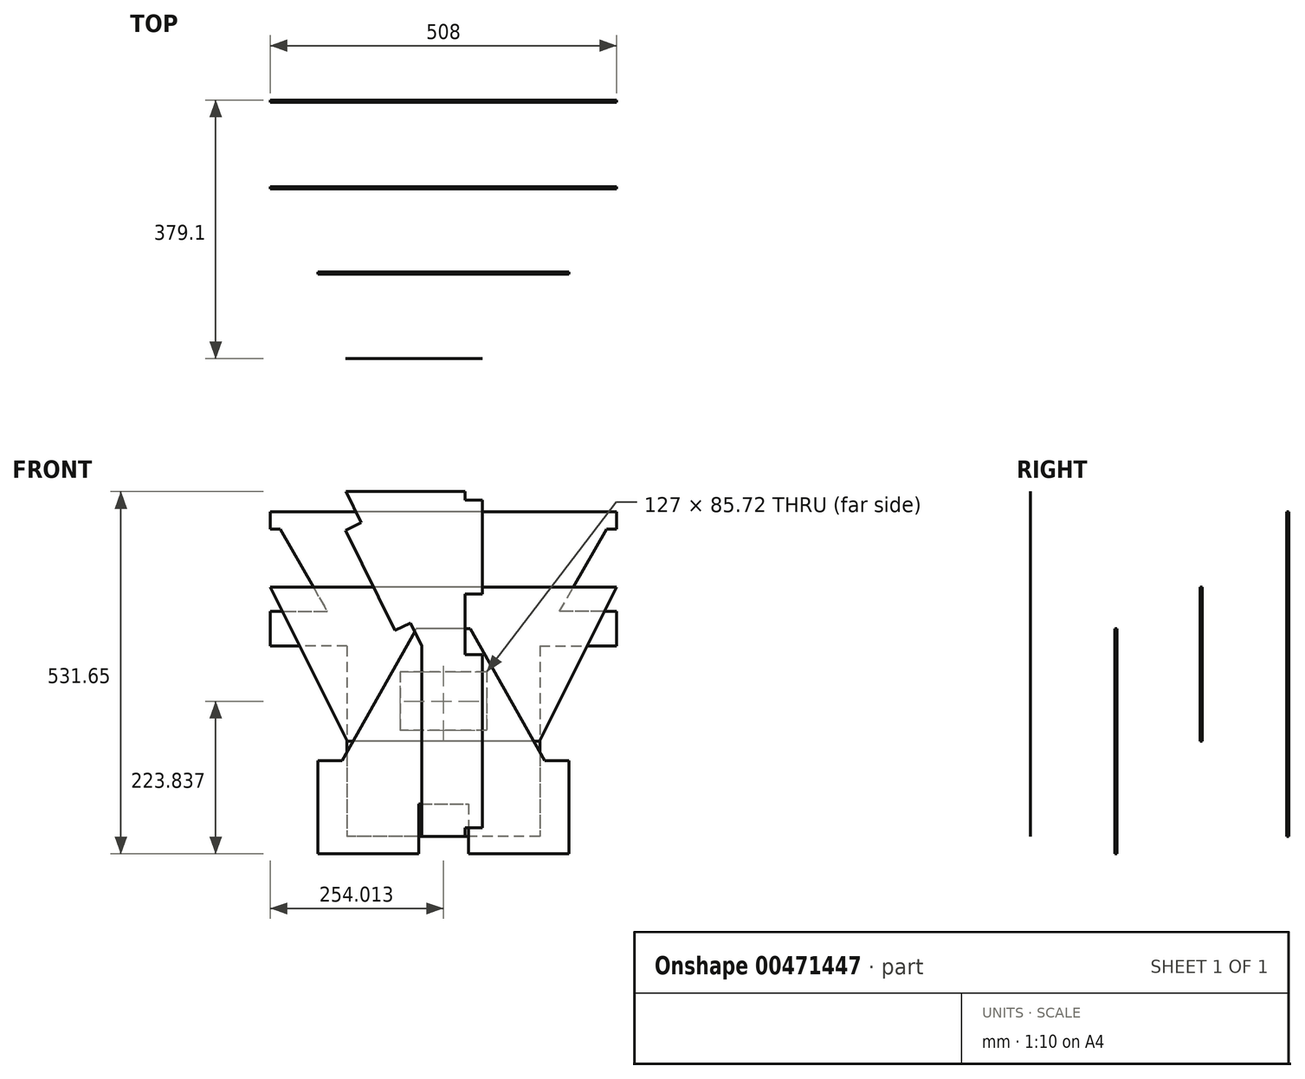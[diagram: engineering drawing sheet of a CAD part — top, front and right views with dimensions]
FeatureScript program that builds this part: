
annotation { "Feature Type Name" : "Feature", "Feature Type Description" : "" }
export const myFeature = defineFeature(function(context is Context, id is Id, definition is map)
    precondition{}
    {
        {
            var Q0;
            Q0=qCreatedBy(makeId("Front.planeOp"),FACE);
            var sketch = newSketch(context, id + "F0", { "sketchPlane" : qUnion([Q0])});
            skPoint(sketch, "E0.middle", {"position": v(0, 0) * mm});
            skLineSegment(sketch, "E1.bottom", {"start": v(-36.51, 165.1) * mm, "end": v(36.51, 165.1) * mm});
            skLineSegment(sketch, "E1.left", {"start": v(-36.51, -92.08) * mm, "end": v(-36.51, -165.1) * mm});
            skLineSegment(sketch, "E1.right", {"start": v(36.51, -92.08) * mm, "end": v(36.51, -165.1) * mm});
            skLineSegment(sketch, "E2", {"start": v(0, 165.1) * mm, "end": v(0, -165.1) * mm, "construction": true});
            skLineSegment(sketch, "E3", {"start": v(-148.48, -28.58) * mm, "end": v(-39.69, 165.1) * mm});
            skLineSegment(sketch, "E4", {"start": v(-36.51, -92.08) * mm, "end": v(36.51, -92.08) * mm});
            skLineSegment(sketch, "E5", {"start": v(-184.15, -92.08) * mm, "end": v(-184.15, -165.1) * mm});
            skLineSegment(sketch, "E6", {"start": v(-184.15, -165.1) * mm, "end": v(-36.51, -165.1) * mm});
            skLineSegment(sketch, "E7", {"start": v(-36.51, -165.1) * mm, "end": v(-36.51, -92.08) * mm});
            skLineSegment(sketch, "E8", {"start": v(-184.15, -92.08) * mm, "end": v(-184.15, -28.58) * mm});
            skLineSegment(sketch, "E9", {"start": v(-184.15, -28.58) * mm, "end": v(-148.48, -28.58) * mm});
            skLineSegment(sketch, "E10.MirrorCS", {"start": v(184.15, -165.1) * mm, "end": v(36.51, -165.1) * mm});
            skLineSegment(sketch, "E11.MirrorCS", {"start": v(36.51, -165.1) * mm, "end": v(36.51, -92.08) * mm});
            skLineSegment(sketch, "E12.MirrorCS", {"start": v(184.15, -92.08) * mm, "end": v(184.15, -165.1) * mm});
            skLineSegment(sketch, "E13.MirrorCS", {"start": v(184.15, -92.08) * mm, "end": v(184.15, -28.58) * mm});
            skLineSegment(sketch, "E14.MirrorCS", {"start": v(148.48, -28.58) * mm, "end": v(39.69, 165.1) * mm});
            skLineSegment(sketch, "E15.MirrorCS", {"start": v(184.15, -28.58) * mm, "end": v(148.48, -28.58) * mm});
            skLineSegment(sketch, "E16.MirrorCS", {"start": v(39.69, 165.1) * mm, "end": v(-39.69, 165.1) * mm});
            skLineSegment(sketch, "E17.MirrorCS", {"start": v(36.51, -92.08) * mm, "end": v(-36.51, -92.08) * mm});
            skPoint(sketch, "E18.MirrorCS.end.orphan", {"position": v(-36.51, -165.1) * mm});
            skPoint(sketch, "E19.orphan", {"position": v(36.51, 165.1) * mm});
            skPoint(sketch, "E20.orphan", {"position": v(-36.51, 165.1) * mm});
            skSolve(sketch);
        }
        {
            var Q0;
            {var subQ1=sQuery(id+"F0.wireOp",EDGE,"E3");Q0=makeQuery(id+"F0.imprint","IMPRINT",FACE,{"disambiguationData":[TD([[makeQuery(id+"F0.imprint","IMPRINT",EDGE,{"derivedFrom":subQ1}),-1.0]])]});}
            extrude(context, id + "F1", {"entities" : qUnion([Q0]), "depth" : 3.17 * mm});
        }
        {
            var Q0;
            Q0=makeQuery(id+"F1.opExtrude","CAP_FACE",FACE,{"disambiguationData":[OSD([sQuery(id+"F0.wireOp",EDGE,"E3"),sQuery(id+"F0.wireOp",EDGE,"E5"),sQuery(id+"F0.wireOp",EDGE,"E6"),sQuery(id+"F0.wireOp",EDGE,"E7"),sQuery(id+"F0.wireOp",EDGE,"E8"),sQuery(id+"F0.wireOp",EDGE,"E9"),sQuery(id+"F0.wireOp",EDGE,"E10.MirrorCS"),sQuery(id+"F0.wireOp",EDGE,"E12.MirrorCS"),sQuery(id+"F0.wireOp",EDGE,"E13.MirrorCS"),sQuery(id+"F0.wireOp",EDGE,"E14.MirrorCS"),sQuery(id+"F0.wireOp",EDGE,"E1.right"),sQuery(id+"F0.wireOp",EDGE,"E15.MirrorCS"),sQuery(id+"F0.wireOp",EDGE,"E16.MirrorCS"),sQuery(id+"F0.wireOp",EDGE,"E17.MirrorCS")])],"isStart":true});
            cPlane(context, id + "F2", {"entities" : qUnion([Q0]), "cplaneType" : CPlaneType.OFFSET, "offset" : 127 * mm, "oppositeDirection" : true, "width" : 152.4 * mm, "height" : 152.4 * mm});
        }
        {
            var Q0;
            Q0=qCreatedBy(id+"F2.planeOp",FACE);
            var sketch = newSketch(context, id + "F3", { "sketchPlane" : qUnion([Q0])});
            skLineSegment(sketch, "E21.bottom", {"start": v(31.75, 139.7) * mm, "end": v(-31.75, 139.7) * mm});
            skLineSegment(sketch, "E21.top", {"start": v(31.75, -139.7) * mm, "end": v(-31.75, -139.7) * mm});
            skLineSegment(sketch, "E21.left", {"start": v(31.75, 139.7) * mm, "end": v(31.75, -139.7) * mm});
            skLineSegment(sketch, "E21.right", {"start": v(-31.75, 139.7) * mm, "end": v(-31.75, -139.7) * mm});
            skPoint(sketch, "E21.middle", {"position": v(0, 0) * mm});
            skLineSegment(sketch, "E22", {"start": v(-31.75, 139.7) * mm, "end": v(-31.75, 366.55) * mm});
            skLineSegment(sketch, "E23", {"start": v(-31.75, 366.55) * mm, "end": v(142.87, 366.55) * mm});
            skLineSegment(sketch, "E24", {"start": v(142.87, 366.55) * mm, "end": v(31.75, 139.7) * mm});
            skLineSegment(sketch, "E25", {"start": v(-31.75, 353.85) * mm, "end": v(-57.15, 353.85) * mm});
            skLineSegment(sketch, "E26", {"start": v(-57.15, 353.85) * mm, "end": v(-57.15, 215.9) * mm});
            skLineSegment(sketch, "E27", {"start": v(-57.15, 215.9) * mm, "end": v(-31.75, 215.9) * mm});
            skLineSegment(sketch, "E28", {"start": v(-31.75, 127) * mm, "end": v(-57.15, 127) * mm});
            skLineSegment(sketch, "E29", {"start": v(-57.15, 127) * mm, "end": v(-57.15, -127) * mm});
            skLineSegment(sketch, "E30", {"start": v(-57.15, -127) * mm, "end": v(-31.75, -127) * mm});
            skLineSegment(sketch, "E31", {"start": v(120.53, 320.93) * mm, "end": v(143.34, 309.75) * mm});
            skLineSegment(sketch, "E32", {"start": v(143.34, 309.75) * mm, "end": v(71.32, 162.74) * mm});
            skLineSegment(sketch, "E33", {"start": v(71.32, 162.74) * mm, "end": v(48.51, 173.92) * mm});
            skSolve(sketch);
        }
        {
            var Q0;
            Q0 = qSketchRegion(id + "F3", true);
            extrude(context, id + "F4", {"entities" : qUnion([Q0]), "depth" : 1 / 203.2 * mm});
        }
        {
            var Q0;
            Q0=makeQuery(id+"F1.opExtrude","CAP_FACE",FACE,{"disambiguationData":[OSD([sQuery(id+"F0.wireOp",EDGE,"E3"),sQuery(id+"F0.wireOp",EDGE,"E5"),sQuery(id+"F0.wireOp",EDGE,"E6"),sQuery(id+"F0.wireOp",EDGE,"E7"),sQuery(id+"F0.wireOp",EDGE,"E8"),sQuery(id+"F0.wireOp",EDGE,"E9"),sQuery(id+"F0.wireOp",EDGE,"E10.MirrorCS"),sQuery(id+"F0.wireOp",EDGE,"E12.MirrorCS"),sQuery(id+"F0.wireOp",EDGE,"E13.MirrorCS"),sQuery(id+"F0.wireOp",EDGE,"E14.MirrorCS"),sQuery(id+"F0.wireOp",EDGE,"E1.right"),sQuery(id+"F0.wireOp",EDGE,"E15.MirrorCS"),sQuery(id+"F0.wireOp",EDGE,"E16.MirrorCS"),sQuery(id+"F0.wireOp",EDGE,"E17.MirrorCS")])],"isStart":true});
            cPlane(context, id + "F5", {"entities" : qUnion([Q0]), "cplaneType" : CPlaneType.OFFSET, "offset" : 121.92 * mm, "width" : 152.4 * mm, "height" : 152.4 * mm});
        }
        {
            var Q0;
            Q0=qCreatedBy(id+"F5.planeOp",FACE);
            var sketch = newSketch(context, id + "F6", { "sketchPlane" : qUnion([Q0])});
            skPoint(sketch, "E34.middle", {"position": v(0, 0) * mm});
            skLineSegment(sketch, "E35", {"start": v(0, 0) * mm, "end": v(0, 226.05) * mm, "construction": true});
            skLineSegment(sketch, "E36", {"start": v(0, 226.05) * mm, "end": v(-254, 226.05) * mm});
            skLineSegment(sketch, "E37", {"start": v(-254, 226.05) * mm, "end": v(-140.92, 0) * mm});
            skLineSegment(sketch, "E38", {"start": v(-140.92, 0) * mm, "end": v(0, 0) * mm});
            skLineSegment(sketch, "E39.MirrorCS", {"start": v(140.92, 0) * mm, "end": v(0, 0) * mm});
            skLineSegment(sketch, "E40.MirrorCS", {"start": v(0, 226.05) * mm, "end": v(254, 226.05) * mm});
            skLineSegment(sketch, "E41.MirrorCS", {"start": v(254, 226.05) * mm, "end": v(140.92, 0) * mm});
            skSolve(sketch);
        }
        {
            var Q0;
            Q0=makeQuery(id+"F6.imprint","IMPRINT",FACE,{"disambiguationData":[TD([[makeQuery(id+"F6.imprint","IMPRINT",EDGE,{"derivedFrom":sQuery(id+"F6.wireOp",EDGE,"E36")}),1.0]])]});
            extrude(context, id + "F7", {"entities" : qUnion([Q0]), "depth" : 3.17 * mm});
        }
        {
            var Q0;
            Q0=qCreatedBy(id+"F5.planeOp",FACE);
            cPlane(context, id + "F8", {"entities" : qUnion([Q0]), "cplaneType" : CPlaneType.OFFSET, "offset" : 127 * mm, "width" : 152.4 * mm, "height" : 152.4 * mm});
        }
        {
            var Q0;
            Q0=qCreatedBy(id+"F8.planeOp",FACE);
            var sketch = newSketch(context, id + "F9", { "sketchPlane" : qUnion([Q0])});
            skLineSegment(sketch, "E42.bottom", {"start": v(-141.29, 139.7) * mm, "end": v(141.29, 139.7) * mm});
            skLineSegment(sketch, "E42.top", {"start": v(-141.29, -139.7) * mm, "end": v(141.29, -139.7) * mm});
            skLineSegment(sketch, "E42.left", {"start": v(-141.29, 139.7) * mm, "end": v(-141.29, -139.7) * mm});
            skLineSegment(sketch, "E42.right", {"start": v(141.29, 139.7) * mm, "end": v(141.29, -139.7) * mm});
            skPoint(sketch, "E42.middle", {"position": v(0, 0) * mm});
            skLineSegment(sketch, "E43", {"start": v(-141.29, 139.7) * mm, "end": v(-254, 336.55) * mm});
            skLineSegment(sketch, "E44", {"start": v(-254, 336.55) * mm, "end": v(254, 336.55) * mm});
            skLineSegment(sketch, "E45", {"start": v(254, 336.55) * mm, "end": v(141.29, 139.7) * mm});
            skLineSegment(sketch, "E46", {"start": v(-63.51, 15.88) * mm, "end": v(-0.01, 15.88) * mm});
            skLineSegment(sketch, "E47", {"start": v(-63.51, 101.6) * mm, "end": v(-0.01, 101.6) * mm});
            skLineSegment(sketch, "E48", {"start": v(0, -139.7) * mm, "end": v(0, 139.7) * mm, "construction": true});
            skLineSegment(sketch, "E49", {"start": v(-0.01, 15.88) * mm, "end": v(63.49, 15.88) * mm});
            skLineSegment(sketch, "E50", {"start": v(-0.01, 101.6) * mm, "end": v(63.49, 101.6) * mm});
            skLineSegment(sketch, "E51", {"start": v(-63.51, 101.6) * mm, "end": v(-63.51, 15.87) * mm});
            skLineSegment(sketch, "E52", {"start": v(63.49, 101.6) * mm, "end": v(63.49, 15.87) * mm});
            skLineSegment(sketch, "E53", {"start": v(-141.29, 139.7) * mm, "end": v(-254, 139.7) * mm});
            skLineSegment(sketch, "E54", {"start": v(-254, 139.7) * mm, "end": v(-254, 190.5) * mm});
            skLineSegment(sketch, "E55", {"start": v(-254, 190.5) * mm, "end": v(-170.37, 190.5) * mm});
            skLineSegment(sketch, "E56", {"start": v(0, 336.55) * mm, "end": v(0, 139.7) * mm, "construction": true});
            skLineSegment(sketch, "E57", {"start": v(-254, 336.55) * mm, "end": v(-254, 190.5) * mm, "construction": true});
            skLineSegment(sketch, "E58.MirrorCS", {"start": v(254, 139.7) * mm, "end": v(254, 190.5) * mm});
            skLineSegment(sketch, "E59.MirrorCS", {"start": v(141.29, 139.7) * mm, "end": v(254, 139.7) * mm});
            skLineSegment(sketch, "E60.MirrorCS", {"start": v(254, 190.5) * mm, "end": v(170.37, 190.5) * mm});
            skLineSegment(sketch, "E61", {"start": v(254, 336.55) * mm, "end": v(254, 311.15) * mm});
            skLineSegment(sketch, "E62", {"start": v(254, 311.15) * mm, "end": v(239.46, 311.15) * mm});
            skLineSegment(sketch, "E63.MirrorCS", {"start": v(-254, 336.55) * mm, "end": v(-254, 311.15) * mm});
            skLineSegment(sketch, "E64.MirrorCS", {"start": v(-254, 311.15) * mm, "end": v(-239.46, 311.15) * mm});
            skSolve(sketch);
        }
        {
            var Q0;
            Q0=makeQuery(id+"F9.imprint","IMPRINT",FACE,{"disambiguationData":[TD([[makeQuery(id+"F9.imprint","IMPRINT",EDGE,{"derivedFrom":sQuery(id+"F9.wireOp",EDGE,"E42.bottom")}),-1.0]])]});
            var Q1;
            Q1=makeQuery(id+"F9.imprint","IMPRINT",FACE,{"disambiguationData":[TD([[makeQuery(id+"F9.imprint","IMPRINT",EDGE,{"derivedFrom":sQuery(id+"F9.wireOp",EDGE,"E42.bottom")}),1.0]])]});
            var Q2;
            {var subQ0=sQuery(id+"F9.wireOp",EDGE,"E53");Q2=makeQuery(id+"F9.imprint","IMPRINT",FACE,{"disambiguationData":[TD([[makeQuery(id+"F9.imprint","IMPRINT",EDGE,{"derivedFrom":subQ0}),-1.0]])]});}
            var Q3;
            Q3=makeQuery(id+"F9.imprint","IMPRINT",FACE,{"disambiguationData":[TD([[makeQuery(id+"F9.imprint","IMPRINT",EDGE,{"derivedFrom":sQuery(id+"F9.wireOp",EDGE,"E58.MirrorCS")}),1.0]])]});
            var Q4;
            {var subQ0=sQuery(id+"F9.wireOp",EDGE,"E61");Q4=makeQuery(id+"F9.imprint","IMPRINT",FACE,{"disambiguationData":[TD([[makeQuery(id+"F9.imprint","IMPRINT",EDGE,{"derivedFrom":subQ0}),-1.0]])]});}
            var Q5;
            {var subQ0=sQuery(id+"F9.wireOp",EDGE,"E63.MirrorCS");Q5=makeQuery(id+"F9.imprint","IMPRINT",FACE,{"disambiguationData":[TD([[makeQuery(id+"F9.imprint","IMPRINT",EDGE,{"derivedFrom":subQ0}),1.0]])]});}
            extrude(context, id + "F10", {"entities" : qUnion([Q0, Q1, Q2, Q3, Q4, Q5]), "depth" : 3.17 * mm});
        }
    });
